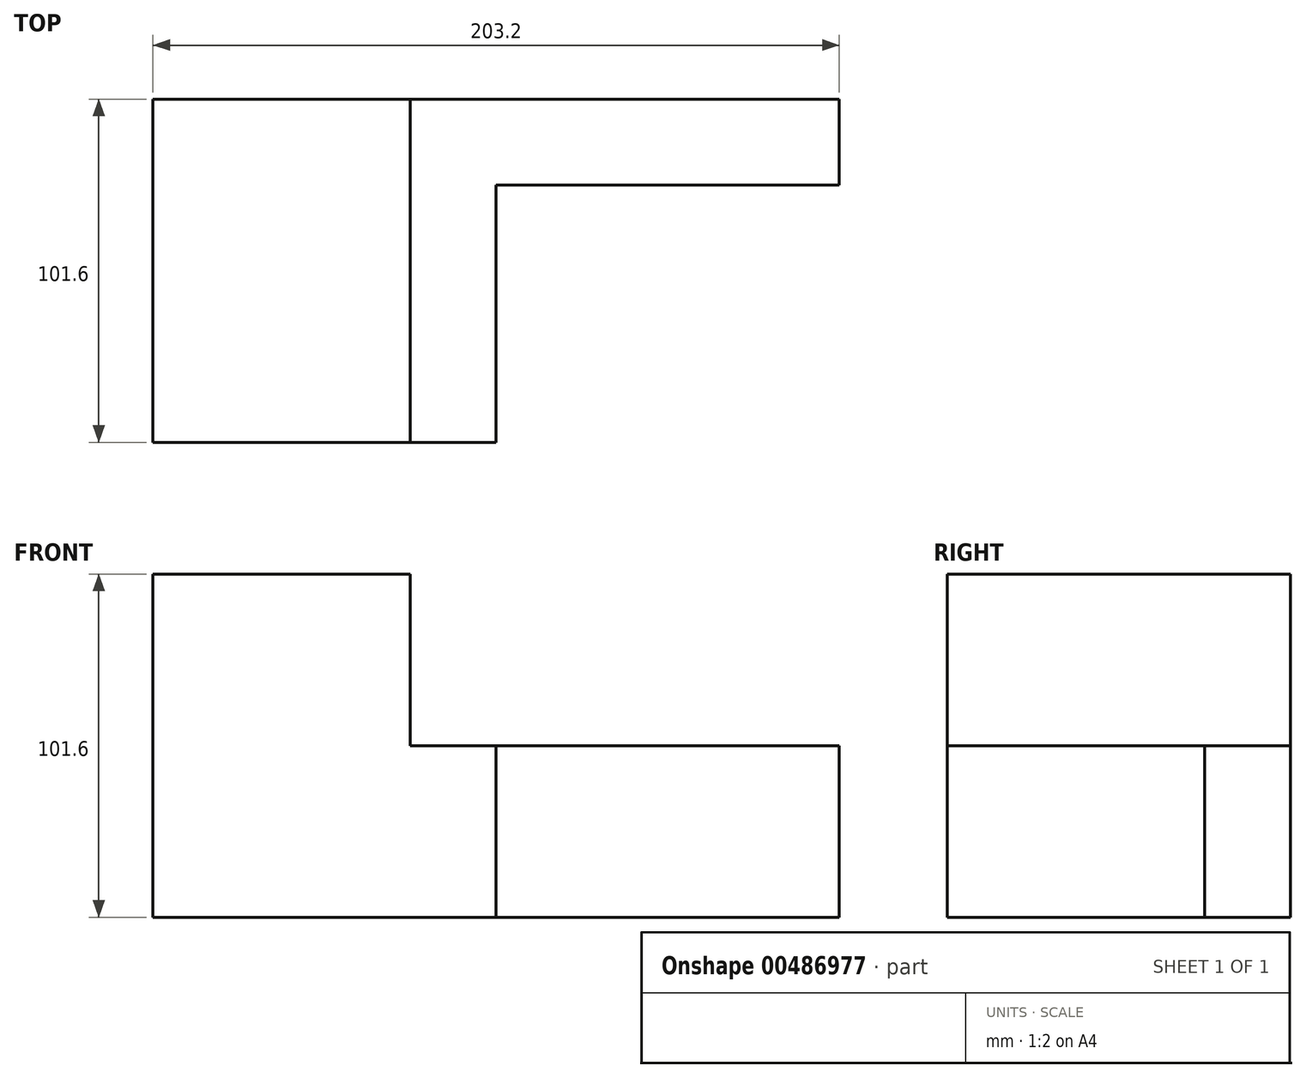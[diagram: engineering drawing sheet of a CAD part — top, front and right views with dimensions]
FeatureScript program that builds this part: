
annotation { "Feature Type Name" : "Feature", "Feature Type Description" : "" }
export const myFeature = defineFeature(function(context is Context, id is Id, definition is map)
    precondition{}
    {
        {
            var Q0;
            Q0=qCreatedBy(makeId("Front.planeOp"),FACE);
            var sketch = newSketch(context, id + "F0", { "sketchPlane" : qUnion([Q0])});
            skLineSegment(sketch, "E0.bottom", {"start": v(0, 0) * mm, "end": v(101.6, 0) * mm});
            skLineSegment(sketch, "E0.top", {"start": v(0, 50.8) * mm, "end": v(101.6, 50.8) * mm});
            skLineSegment(sketch, "E0.left", {"start": v(0, 0) * mm, "end": v(0, 50.8) * mm});
            skLineSegment(sketch, "E0.right", {"start": v(101.6, 0) * mm, "end": v(101.6, 50.8) * mm});
            skLineSegment(sketch, "E1.bottom", {"start": v(0, 0) * mm, "end": v(-25.4, 0) * mm});
            skLineSegment(sketch, "E1.top", {"start": v(0, 50.8) * mm, "end": v(-25.4, 50.8) * mm});
            skLineSegment(sketch, "E2.bottom", {"start": v(-25.4, 0) * mm, "end": v(-101.6, 0) * mm});
            skLineSegment(sketch, "E2.top", {"start": v(-25.4, 101.6) * mm, "end": v(-101.6, 101.6) * mm});
            skLineSegment(sketch, "E2.left", {"start": v(-25.4, 50.8) * mm, "end": v(-25.4, 101.6) * mm});
            skLineSegment(sketch, "E2.right", {"start": v(-101.6, 0) * mm, "end": v(-101.6, 101.6) * mm});
            skSolve(sketch);
        }
        {
            var Q0;
            Q0=makeQuery(id+"F0.imprint","IMPRINT",FACE,{"disambiguationData":[TD([[makeQuery(id+"F0.imprint","IMPRINT",EDGE,{"derivedFrom":sQuery(id+"F0.wireOp",EDGE,"E0.bottom")}),1.0]])]});
            extrude(context, id + "F1", {"entities" : qUnion([Q0]), "depth" : 25.4 * mm});
        }
        {
            var Q0;
            Q0 = qSketchRegion(id + "F0", true);
            extrude(context, id + "F2", {"entities" : qUnion([Q0]), "operationType" : NewBodyOperationType.ADD, "depth" : 101.6 * mm});
        }
        {
            var Q0;
            {var subQ0=sQuery(id+"F0.wireOp",EDGE,"E0.top");Q0=makeQuery(id+"F2.boolean.opBoolean","MERGE",FACE,{"derivedFrom":[makeQuery(id+"F1.opExtrude","SWEPT_FACE",FACE,{"disambiguationData":[OSD([subQ0])]}),makeQuery(id+"F2.opExtrude","SWEPT_FACE",FACE,{"disambiguationData":[OSD([subQ0,sQuery(id+"F0.wireOp",EDGE,"E1.top")])]})]});}
            var sketch = newSketch(context, id + "F3", { "sketchPlane" : qUnion([Q0])});
            skLineSegment(sketch, "E3.bottom", {"start": v(101.6, -101.6) * mm, "end": v(0, -101.6) * mm});
            skLineSegment(sketch, "E3.top", {"start": v(101.6, -25.4) * mm, "end": v(0, -25.4) * mm});
            skLineSegment(sketch, "E3.left", {"start": v(101.6, -101.6) * mm, "end": v(101.6, -25.4) * mm});
            skLineSegment(sketch, "E3.right", {"start": v(0, -101.6) * mm, "end": v(0, -25.4) * mm});
            skSolve(sketch);
        }
        {
            var Q0;
            Q0=makeQuery(id+"F3.imprint","IMPRINT",FACE,{"disambiguationData":[TD([[makeQuery(id+"F3.imprint","IMPRINT",EDGE,{"derivedFrom":sQuery(id+"F3.wireOp",EDGE,"E3.bottom")}),1.0]])]});
            extrude(context, id + "F4", {"entities" : qUnion([Q0]), "operationType" : NewBodyOperationType.REMOVE, "oppositeDirection" : true, "depth" : 50.8 * mm});
        }
    });
